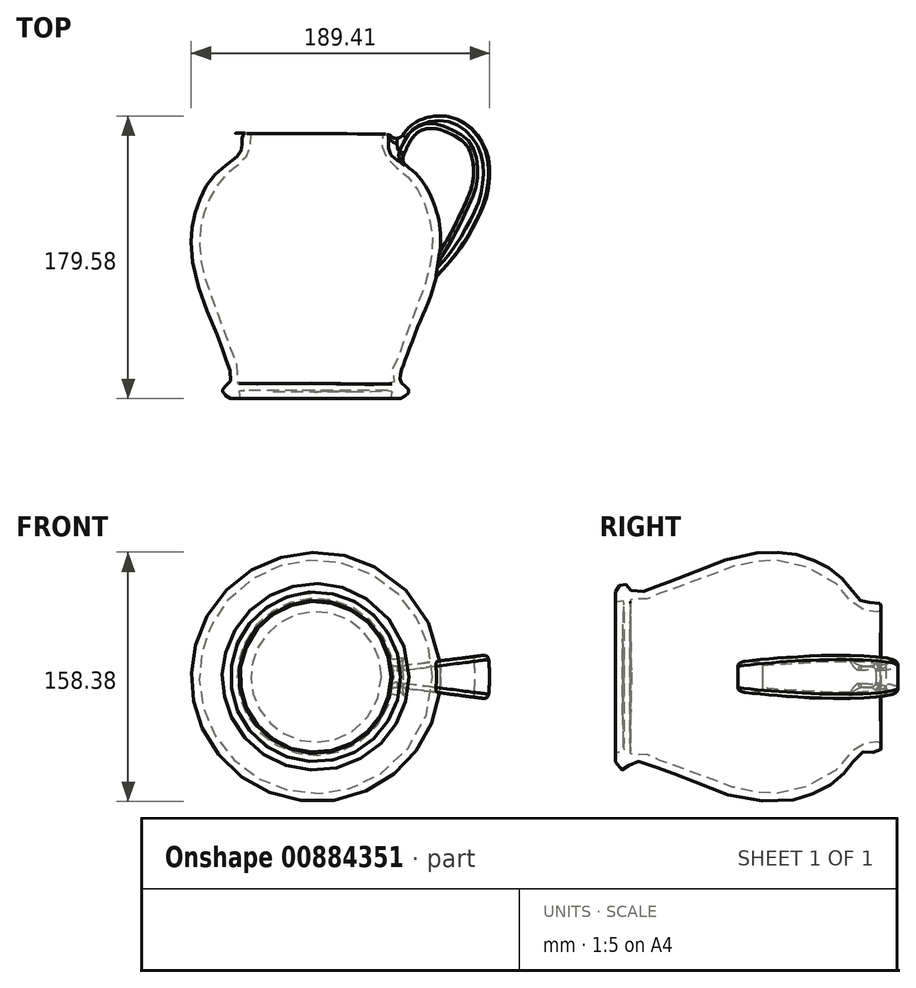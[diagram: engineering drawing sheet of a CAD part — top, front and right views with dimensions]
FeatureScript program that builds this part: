
annotation { "Feature Type Name" : "Feature", "Feature Type Description" : "" }
export const myFeature = defineFeature(function(context is Context, id is Id, definition is map)
    precondition{}
    {
        {
            var Q0;
            Q0=qCreatedBy(makeId("Top.planeOp"),FACE);
            var sketch = newSketch(context, id + "F0", { "sketchPlane" : qUnion([Q0])});
            skFitSpline(sketch, "E0", {"points": [v(149.3, -82.28) * mm, v(144.46, -76.94) * mm, v(144.46, -69.81) * mm, v(148.02, -59.9) * mm, v(154.89, -41.84) * mm, v(161, -27.34) * mm, v(166.59, -10.55) * mm, v(169.13, 5.47) * mm, v(168.62, 24.29) * mm, v(163.28, 41.07) * mm, v(155.4, 53.8) * mm, v(142.43, 64.73) * mm, v(137.85, 70.58) * mm, v(136.83, 80.83) * mm, v(134.54, 80.83) * mm, v(132.5, 80.83) * mm, v(132.25, 73.37) * mm, v(134.54, 66.76) * mm, v(139.63, 60.91) * mm, v(146.24, 55.83) * mm, v(153.36, 47.69) * mm, v(158.45, 38.28) * mm, v(162.27, 27.09) * mm, v(164.3, 15.39) * mm, v(163.54, 2.67) * mm, v(160.74, -11.32) * mm, v(155.4, -25.56) * mm, v(150.57, -39.04) * mm, v(145.23, -53.03) * mm, v(140.9, -64.73) * mm, v(138.61, -70.58) * mm, v(139.88, -77.44) * mm, v(137.85, -77.95) * mm, v(127.42, -78.2) * mm, v(112.92, -77.7) * mm, v(98.68, -77.44) * mm, v(89.27, -77.7) * mm, v(89.53, -79.22) * mm, v(89.53, -82.53) * mm, v(96.14, -82.53) * mm, v(110.9, -82.78) * mm, v(129.97, -82.53) * mm, v(138.36, -82.78) * mm, v(138.1, -84.57) * mm, v(138.36, -87.1) * mm, v(143.95, -87.36) * mm, v(149.3, -82.28) * mm]});
            skLineSegment(sketch, "E1", {"start": v(36.08, -87.1) * mm, "end": v(143.95, -87.36) * mm});
            skLineSegment(sketch, "E2", {"start": v(90.02, -89.83) * mm, "end": v(90.46, 90.8) * mm});
            skPoint(sketch, "E2.startSnap0", {"position": v(90.02, -87.23) * mm});
            skSolve(sketch);
        }
        {
            var Q0;
            Q0=qCreatedBy(makeId("Top.planeOp"),FACE);
            var sketch = newSketch(context, id + "F1", { "sketchPlane" : qUnion([Q0])});
            skFitSpline(sketch, "E3", {"points": [v(162.27, -14.37) * mm, v(175.74, 0) * mm, v(185.16, 12.84) * mm, v(195.07, 31.16) * mm, v(199.4, 44.64) * mm, v(199.9, 64.47) * mm, v(194.57, 77.7) * mm, v(187.7, 85.58) * mm, v(181.6, 89.4) * mm, v(176, 91.43) * mm, v(167.86, 92.2) * mm, v(159.47, 90.67) * mm, v(151.33, 86.6) * mm, v(145.23, 79.73) * mm, v(141.16, 71.6) * mm, v(138.87, 64.73) * mm, v(138.87, 64.98) * mm], "startDerivative": vector(166.04, 170.23) * mm, "endDerivative": vector(3.44, 39.55) * mm});
            skLineSegment(sketch, "E4", {"start": v(138.87, 64.98) * mm, "end": v(143.43, 60.68) * mm});
            skFitSpline(sketch, "E5", {"points": [v(143.43, 60.68) * mm, v(147.22, 70.08) * mm, v(151.92, 78.62) * mm, v(157.42, 83.1) * mm, v(165.54, 84.3) * mm, v(173.83, 81.89) * mm, v(183.74, 76.36) * mm, v(188.9, 69.1) * mm, v(190.9, 54.47) * mm, v(187.08, 40.07) * mm, v(179.57, 24.11) * mm, v(173.4, 12.6) * mm, v(166.02, 0) * mm, v(162.27, -14.37) * mm], "startDerivative": vector(50.18, 130.73) * mm, "endDerivative": vector(-30.89, -169.5) * mm});
            skSolve(sketch);
        }
        {
            var Q0;
            {var subQ0=sQuery(id+"F0.wireOp",EDGE,"E2");var subQ1=sQuery(id+"F0.wireOp",EDGE,"E0");var subQ2=makeQuery(id+"F0.imprint","INTERSECT",VERTEX,{"disambiguationData":[OD(1.0)],"derivedFrom":[subQ1,subQ0]});Q0=makeQuery(id+"F0.imprint","IMPRINT",FACE,{"disambiguationData":[TD([[makeQuery(id+"F0.imprint","IMPRINT",EDGE,{"disambiguationData":[TD([[subQ2,-1.0]])],"derivedFrom":subQ1}),1.0]])]});}
            var Q1;
            Q1=sQuery(id+"F0.wireOp",EDGE,"E0");
            var Q2;
            Q2=sQuery(id+"F0.wireOp",EDGE,"E2");
            revolve(context, id + "F2", {"surfaceOperationType" : NewSurfaceOperationType.ADD, "entities" : qUnion([Q0]), "surfaceEntities" : qUnion([Q1]), "axis" : qUnion([Q2]), "revolveType" : RevolveType.FULL});
        }
        {
            var Q0;
            {var subQ0=sQuery(id+"F1.wireOp",EDGE,"E5");Q0=makeQuery(id+"F1.imprint","IMPRINT",FACE,{"disambiguationData":[TD([[makeQuery(id+"F1.imprint","IMPRINT",EDGE,{"derivedFrom":subQ0}),1.0]])]});}
            var Q1;
            Q1=sQuery(id+"F1.wireOp",EDGE,"E3");
            var Q2;
            Q2=sQuery(id+"F1.wireOp",EDGE,"E5");
            var Q3;
            Q3=sQuery(id+"F1.wireOp",EDGE,"E4");
            var Q4;
            {var subQ0=sQuery(id+"F0.wireOp",EDGE,"E0");Q4=makeQuery(id+"F2.opRevolve","SWEPT_FACE",FACE,{"disambiguationData":[OSD([subQ0]),TDD([makeQuery(id+"F0.imprint","IMPRINT",EDGE,{"disambiguationData":[TD([[makeQuery(id+"F0.imprint","INTERSECT",VERTEX,{"disambiguationData":[OD(0.0)],"derivedFrom":[subQ0,sQuery(id+"F0.wireOp",EDGE,"E1")]}),-1.0]])],"derivedFrom":subQ0})])]});}
            revolve(context, id + "F3", {"operationType" : NewBodyOperationType.ADD, "surfaceOperationType" : NewSurfaceOperationType.NEW, "entities" : qUnion([Q0]), "surfaceEntities" : qUnion([Q1, Q2, Q3]), "axis" : qUnion([Q4]), "revolveType" : RevolveType.SYMMETRIC, "angle" : 14.66 * degree});
        }
        {
            var Q0;
            {var subQ0=sQuery(id+"F0.wireOp",EDGE,"E0");Q0=makeQuery(id+"F3.boolean.opBoolean","INTERSECT",EDGE,{"disambiguationData":[OD(1.0)],"derivedFrom":[makeQuery(id+"F2.opRevolve","SWEPT_FACE",FACE,{"disambiguationData":[OSD([subQ0]),TDD([makeQuery(id+"F0.imprint","IMPRINT",EDGE,{"disambiguationData":[TD([[makeQuery(id+"F0.imprint","INTERSECT",VERTEX,{"disambiguationData":[OD(0.0)],"derivedFrom":[subQ0,sQuery(id+"F0.wireOp",EDGE,"E1")]}),-1.0]])],"derivedFrom":subQ0})])]}),makeQuery(id+"F3.opRevolve","SWEPT_FACE",FACE,{"disambiguationData":[OSD([sQuery(id+"F1.wireOp",EDGE,"E3")])]})]});}
            var Q1;
            {var subQ0=sQuery(id+"F0.wireOp",EDGE,"E0");Q1=makeQuery(id+"F3.boolean.opBoolean","INTERSECT",EDGE,{"disambiguationData":[OD(1.0)],"derivedFrom":[makeQuery(id+"F2.opRevolve","SWEPT_FACE",FACE,{"disambiguationData":[OSD([subQ0]),TDD([makeQuery(id+"F0.imprint","IMPRINT",EDGE,{"disambiguationData":[TD([[makeQuery(id+"F0.imprint","INTERSECT",VERTEX,{"disambiguationData":[OD(0.0)],"derivedFrom":[subQ0,sQuery(id+"F0.wireOp",EDGE,"E1")]}),-1.0]])],"derivedFrom":subQ0})])]}),makeQuery(id+"F3.opRevolve","CAP_FACE",FACE,{"disambiguationData":[OSD([sQuery(id+"F1.wireOp",EDGE,"E3"),sQuery(id+"F1.wireOp",EDGE,"E4"),sQuery(id+"F1.wireOp",EDGE,"E5")])],"isStart":false})]});}
            var Q2;
            {var subQ0=sQuery(id+"F0.wireOp",EDGE,"E0");Q2=makeQuery(id+"F3.boolean.opBoolean","INTERSECT",EDGE,{"disambiguationData":[OD(1.0)],"derivedFrom":[makeQuery(id+"F2.opRevolve","SWEPT_FACE",FACE,{"disambiguationData":[OSD([subQ0]),TDD([makeQuery(id+"F0.imprint","IMPRINT",EDGE,{"disambiguationData":[TD([[makeQuery(id+"F0.imprint","INTERSECT",VERTEX,{"disambiguationData":[OD(0.0)],"derivedFrom":[subQ0,sQuery(id+"F0.wireOp",EDGE,"E1")]}),-1.0]])],"derivedFrom":subQ0})])]}),makeQuery(id+"F3.opRevolve","SWEPT_FACE",FACE,{"disambiguationData":[OSD([sQuery(id+"F1.wireOp",EDGE,"E5")])]})]});}
            var Q3;
            {var subQ0=sQuery(id+"F0.wireOp",EDGE,"E0");Q3=makeQuery(id+"F3.boolean.opBoolean","INTERSECT",EDGE,{"disambiguationData":[OD(1.0)],"derivedFrom":[makeQuery(id+"F2.opRevolve","SWEPT_FACE",FACE,{"disambiguationData":[OSD([subQ0]),TDD([makeQuery(id+"F0.imprint","IMPRINT",EDGE,{"disambiguationData":[TD([[makeQuery(id+"F0.imprint","INTERSECT",VERTEX,{"disambiguationData":[OD(0.0)],"derivedFrom":[subQ0,sQuery(id+"F0.wireOp",EDGE,"E1")]}),-1.0]])],"derivedFrom":subQ0})])]}),makeQuery(id+"F3.opRevolve","CAP_FACE",FACE,{"disambiguationData":[OSD([sQuery(id+"F1.wireOp",EDGE,"E3"),sQuery(id+"F1.wireOp",EDGE,"E4"),sQuery(id+"F1.wireOp",EDGE,"E5")])],"isStart":true})]});}
            fillet(context, id + "F4", {"entities" : qUnion([Q0, Q1, Q2, Q3]), "radius" : 5 * mm, "tangentPropagation" : true, "allowEdgeOverflow" : false});
        }
        {
            var Q0;
            Q0=makeQuery(id+"F3.opRevolve","CAP_EDGE",EDGE,{"disambiguationData":[OSD([sQuery(id+"F1.wireOp",EDGE,"E5")])],"isStart":false});
            var Q1;
            Q1=makeQuery(id+"F3.opRevolve","CAP_EDGE",EDGE,{"disambiguationData":[OSD([sQuery(id+"F1.wireOp",EDGE,"E3")])],"isStart":false});
            var Q2;
            Q2=makeQuery(id+"F3.opRevolve","CAP_EDGE",EDGE,{"disambiguationData":[OSD([sQuery(id+"F1.wireOp",EDGE,"E3")])],"isStart":true});
            var Q3;
            Q3=makeQuery(id+"F3.opRevolve","CAP_EDGE",EDGE,{"disambiguationData":[OSD([sQuery(id+"F1.wireOp",EDGE,"E5")])],"isStart":true});
            fillet(context, id + "F5", {"entities" : qUnion([Q0, Q1, Q2, Q3]), "radius" : 3 * mm, "tangentPropagation" : true, "allowEdgeOverflow" : false});
        }
    });
